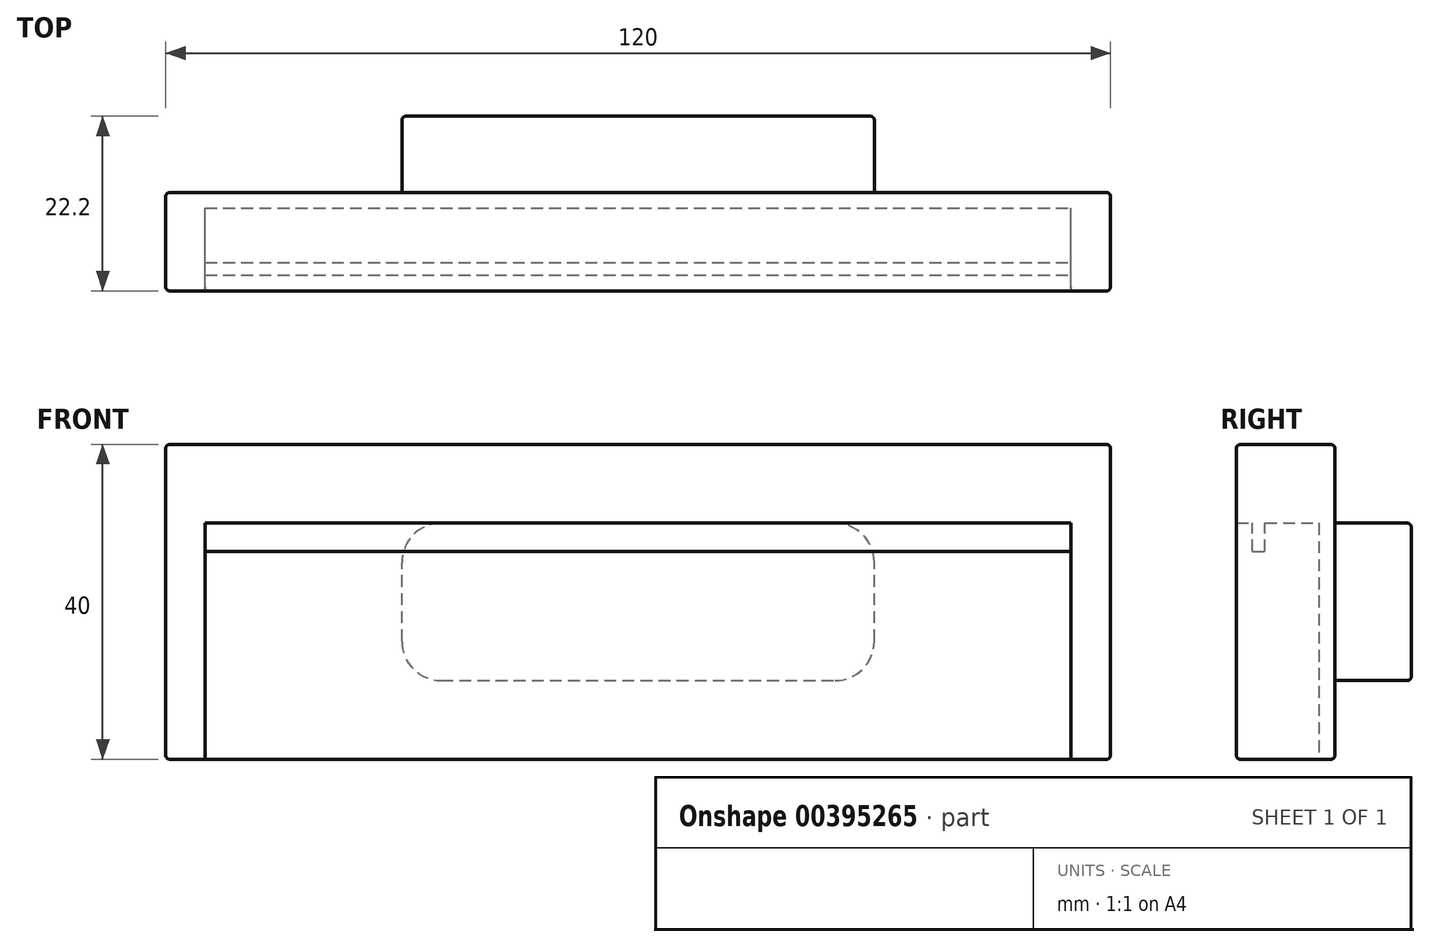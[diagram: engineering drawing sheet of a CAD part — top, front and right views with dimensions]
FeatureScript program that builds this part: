
annotation { "Feature Type Name" : "Feature", "Feature Type Description" : "" }
export const myFeature = defineFeature(function(context is Context, id is Id, definition is map)
    precondition{}
    {
        {
            var Q0;
            Q0=qCreatedBy(makeId("Front.planeOp"),FACE);
            var sketch = newSketch(context, id + "F0", { "sketchPlane" : qUnion([Q0])});
            skLineSegment(sketch, "E0.bottom", {"start": v(60, -20) * mm, "end": v(-60, -20) * mm});
            skLineSegment(sketch, "E0.top", {"start": v(60, 20) * mm, "end": v(-60, 20) * mm});
            skLineSegment(sketch, "E0.left", {"start": v(60, -20) * mm, "end": v(60, 20) * mm});
            skLineSegment(sketch, "E0.right", {"start": v(-60, -20) * mm, "end": v(-60, 20) * mm});
            skPoint(sketch, "E0.middle", {"position": v(0, 0) * mm});
            skSolve(sketch);
        }
        {
            var Q0;
            Q0 = qSketchRegion(id + "F0", true);
            extrude(context, id + "F1", {"entities" : qUnion([Q0]), "depth" : 12.5 * mm});
        }
        {
            var Q0;
            Q0=makeQuery(id+"F1.opExtrude","CAP_FACE",FACE,{"disambiguationData":[OSD([sQuery(id+"F0.wireOp",EDGE,"E0.bottom"),sQuery(id+"F0.wireOp",EDGE,"E0.top"),sQuery(id+"F0.wireOp",EDGE,"E0.left"),sQuery(id+"F0.wireOp",EDGE,"E0.right")])],"isStart":true});
            var sketch = newSketch(context, id + "F2", { "sketchPlane" : qUnion([Q0])});
            skLineSegment(sketch, "E1.bottom", {"start": v(25, -10) * mm, "end": v(-25, -10) * mm});
            skLineSegment(sketch, "E1.top", {"start": v(25, 10) * mm, "end": v(-25, 10) * mm});
            skLineSegment(sketch, "E1.left", {"start": v(30, -5) * mm, "end": v(30, 5) * mm});
            skLineSegment(sketch, "E1.right", {"start": v(-30, -5) * mm, "end": v(-30, 5) * mm});
            skPoint(sketch, "E1.middle", {"position": v(0, 0) * mm});
            skPoint(sketch, "E2.visualSharp", {"position": v(-30, 10) * mm});
            skArc(sketch, "E2.filletArc", {"start": v(-25, 10) * mm, "mid": v(-28.54, 8.54) * mm, "end": v(-30, 5) * mm});
            skPoint(sketch, "E3.visualSharp", {"position": v(-30, -10) * mm});
            skArc(sketch, "E3.filletArc", {"start": v(-30, -5) * mm, "mid": v(-28.54, -8.54) * mm, "end": v(-25, -10) * mm});
            skPoint(sketch, "E4.visualSharp", {"position": v(30, -10) * mm});
            skArc(sketch, "E4.filletArc", {"start": v(25, -10) * mm, "mid": v(28.54, -8.54) * mm, "end": v(30, -5) * mm});
            skPoint(sketch, "E5.visualSharp", {"position": v(30, 10) * mm});
            skArc(sketch, "E5.filletArc", {"start": v(30, 5) * mm, "mid": v(28.54, 8.54) * mm, "end": v(25, 10) * mm});
            skSolve(sketch);
        }
        {
            var Q0;
            Q0 = qSketchRegion(id + "F2", true);
            extrude(context, id + "F3", {"entities" : qUnion([Q0]), "operationType" : NewBodyOperationType.ADD, "depth" : 9.7 * mm});
        }
        {
            var Q0;
            Q0=makeQuery(id+"F1.opExtrude","SWEPT_FACE",FACE,{"disambiguationData":[OSD([sQuery(id+"F0.wireOp",EDGE,"E0.bottom")])]});
            var sketch = newSketch(context, id + "F4", { "sketchPlane" : qUnion([Q0])});
            skLineSegment(sketch, "E6.bottom", {"start": v(-55, 12.5) * mm, "end": v(55, 12.5) * mm});
            skLineSegment(sketch, "E6.top", {"start": v(-55, 2) * mm, "end": v(55, 2) * mm});
            skLineSegment(sketch, "E6.left", {"start": v(-55, 12.5) * mm, "end": v(-55, 2) * mm});
            skLineSegment(sketch, "E6.right", {"start": v(55, 12.5) * mm, "end": v(55, 2) * mm});
            skSolve(sketch);
        }
        {
            var Q0;
            Q0 = qSketchRegion(id + "F4", true);
            extrude(context, id + "F5", {"entities" : qUnion([Q0]), "operationType" : NewBodyOperationType.REMOVE, "oppositeDirection" : true, "depth" : 30 * mm});
        }
        {
            var Q0;
            Q0=makeQuery(id+"F5.boolean.opBoolean","COPY",FACE,{"derivedFrom":makeQuery(id+"F5.opExtrude","CAP_FACE",FACE,{"disambiguationData":[OSD([sQuery(id+"F4.wireOp",EDGE,"E6.bottom"),sQuery(id+"F4.wireOp",EDGE,"E6.top"),sQuery(id+"F4.wireOp",EDGE,"E6.left"),sQuery(id+"F4.wireOp",EDGE,"E6.right")])],"isStart":false})});
            var sketch = newSketch(context, id + "F6", { "sketchPlane" : qUnion([Q0])});
            skLineSegment(sketch, "E7.bottom", {"start": v(-55, 10.48) * mm, "end": v(55, 10.48) * mm});
            skLineSegment(sketch, "E7.top", {"start": v(-55, 8.86) * mm, "end": v(55, 8.86) * mm});
            skLineSegment(sketch, "E7.left", {"start": v(-55, 10.48) * mm, "end": v(-55, 8.86) * mm});
            skLineSegment(sketch, "E7.right", {"start": v(55, 10.48) * mm, "end": v(55, 8.86) * mm});
            skLineSegment(sketch, "E8", {"start": v(-55, 9.67) * mm, "end": v(55, 9.67) * mm, "construction": true});
            skSolve(sketch);
        }
        {
            var Q0;
            Q0 = qSketchRegion(id + "F6", true);
            extrude(context, id + "F7", {"entities" : qUnion([Q0]), "operationType" : NewBodyOperationType.ADD, "depth" : 3.6 * mm});
        }
        {
            var Q0;
            Q0=makeQuery(id+"F3.opExtrude","CAP_EDGE",EDGE,{"disambiguationData":[OSD([sQuery(id+"F2.wireOp",EDGE,"E1.bottom")])],"isStart":false});
            var Q1;
            Q1=makeQuery(id+"F5.boolean.opBoolean","COPY",EDGE,{"derivedFrom":makeQuery(id+"F5.opExtrude","CAP_EDGE",EDGE,{"disambiguationData":[OSD([sQuery(id+"F4.wireOp",EDGE,"E6.top")])],"isStart":true})});
            var Q2;
            Q2=makeQuery(id+"F5.boolean.opBoolean","COPY",EDGE,{"derivedFrom":makeQuery(id+"F5.opExtrude","CAP_EDGE",EDGE,{"disambiguationData":[OSD([sQuery(id+"F4.wireOp",EDGE,"E6.right")])],"isStart":true})});
            var Q3;
            Q3=makeQuery(id+"F5.boolean.opBoolean","COPY",EDGE,{"derivedFrom":makeQuery(id+"F5.opExtrude","SWEPT_EDGE",EDGE,{"disambiguationData":[OSD([sQuery(id+"F0.wireOp",EDGE,"E0.bottom"),sQuery(id+"F4.wireOp",EDGE,"E6.bottom"),sQuery(id+"F4.wireOp",EDGE,"E6.right")])]})});
            var Q4;
            Q4=makeQuery(id+"F5.boolean.opBoolean","COPY",EDGE,{"derivedFrom":makeQuery(id+"F5.opExtrude","CAP_EDGE",EDGE,{"disambiguationData":[OSD([sQuery(id+"F4.wireOp",EDGE,"E6.bottom")])],"isStart":false})});
            var Q5;
            Q5=makeQuery(id+"F5.boolean.opBoolean","COPY",EDGE,{"derivedFrom":makeQuery(id+"F5.opExtrude","SWEPT_EDGE",EDGE,{"disambiguationData":[OSD([sQuery(id+"F0.wireOp",EDGE,"E0.bottom"),sQuery(id+"F4.wireOp",EDGE,"E6.bottom"),sQuery(id+"F4.wireOp",EDGE,"E6.left")])]})});
            var Q6;
            Q6=makeQuery(id+"F5.boolean.opBoolean","COPY",EDGE,{"derivedFrom":makeQuery(id+"F5.opExtrude","CAP_EDGE",EDGE,{"disambiguationData":[OSD([sQuery(id+"F4.wireOp",EDGE,"E6.left")])],"isStart":true})});
            var Q7;
            {var subQ0=sQuery(id+"F0.wireOp",EDGE,"E0.bottom");var subQ1=sQuery(id+"F0.wireOp",EDGE,"E0.left");Q7=makeQuery(id+"F5.boolean.opBoolean","SPLIT",EDGE,{"disambiguationData":[TD([makeQuery(id+"F1.opExtrude","SWEPT_FACE",FACE,{"disambiguationData":[OSD([subQ1])]})])],"derivedFrom":makeQuery(id+"F1.opExtrude","CAP_EDGE",EDGE,{"disambiguationData":[OSD([subQ0])],"isStart":false})});}
            var Q8;
            Q8=makeQuery(id+"F1.opExtrude","CAP_EDGE",EDGE,{"disambiguationData":[OSD([sQuery(id+"F0.wireOp",EDGE,"E0.left")])],"isStart":false});
            var Q9;
            Q9=makeQuery(id+"F1.opExtrude","CAP_EDGE",EDGE,{"disambiguationData":[OSD([sQuery(id+"F0.wireOp",EDGE,"E0.top")])],"isStart":false});
            var Q10;
            Q10=makeQuery(id+"F1.opExtrude","CAP_EDGE",EDGE,{"disambiguationData":[OSD([sQuery(id+"F0.wireOp",EDGE,"E0.right")])],"isStart":false});
            var Q11;
            {var subQ0=sQuery(id+"F0.wireOp",EDGE,"E0.bottom");var subQ1=sQuery(id+"F0.wireOp",EDGE,"E0.right");Q11=makeQuery(id+"F5.boolean.opBoolean","SPLIT",EDGE,{"disambiguationData":[TD([makeQuery(id+"F1.opExtrude","SWEPT_FACE",FACE,{"disambiguationData":[OSD([subQ1])]})])],"derivedFrom":makeQuery(id+"F1.opExtrude","CAP_EDGE",EDGE,{"disambiguationData":[OSD([subQ0])],"isStart":false})});}
            var Q12;
            Q12=makeQuery(id+"F1.opExtrude","SWEPT_EDGE",EDGE,{"disambiguationData":[OSD([sQuery(id+"F0.wireOp",EDGE,"E0.bottom"),sQuery(id+"F0.wireOp",EDGE,"E0.left")])]});
            var Q13;
            Q13=makeQuery(id+"F1.opExtrude","SWEPT_EDGE",EDGE,{"disambiguationData":[OSD([sQuery(id+"F0.wireOp",EDGE,"E0.top"),sQuery(id+"F0.wireOp",EDGE,"E0.left")])]});
            var Q14;
            Q14=makeQuery(id+"F1.opExtrude","SWEPT_EDGE",EDGE,{"disambiguationData":[OSD([sQuery(id+"F0.wireOp",EDGE,"E0.top"),sQuery(id+"F0.wireOp",EDGE,"E0.right")])]});
            var Q15;
            Q15=makeQuery(id+"F1.opExtrude","SWEPT_EDGE",EDGE,{"disambiguationData":[OSD([sQuery(id+"F0.wireOp",EDGE,"E0.bottom"),sQuery(id+"F0.wireOp",EDGE,"E0.right")])]});
            var Q16;
            Q16=makeQuery(id+"F1.opExtrude","CAP_EDGE",EDGE,{"disambiguationData":[OSD([sQuery(id+"F0.wireOp",EDGE,"E0.right")])],"isStart":true});
            var Q17;
            Q17=makeQuery(id+"F1.opExtrude","CAP_EDGE",EDGE,{"disambiguationData":[OSD([sQuery(id+"F0.wireOp",EDGE,"E0.top")])],"isStart":true});
            var Q18;
            Q18=makeQuery(id+"F1.opExtrude","CAP_EDGE",EDGE,{"disambiguationData":[OSD([sQuery(id+"F0.wireOp",EDGE,"E0.bottom")])],"isStart":true});
            var Q19;
            Q19=makeQuery(id+"F1.opExtrude","CAP_EDGE",EDGE,{"disambiguationData":[OSD([sQuery(id+"F0.wireOp",EDGE,"E0.left")])],"isStart":true});
            fillet(context, id + "F8", {"entities" : qUnion([Q0, Q1, Q2, Q3, Q4, Q5, Q6, Q7, Q8, Q9, Q10, Q11, Q12, Q13, Q14, Q15, Q16, Q17, Q18, Q19]), "radius" : 0.5 * mm, "tangentPropagation" : true, "allowEdgeOverflow" : false});
        }
    });
